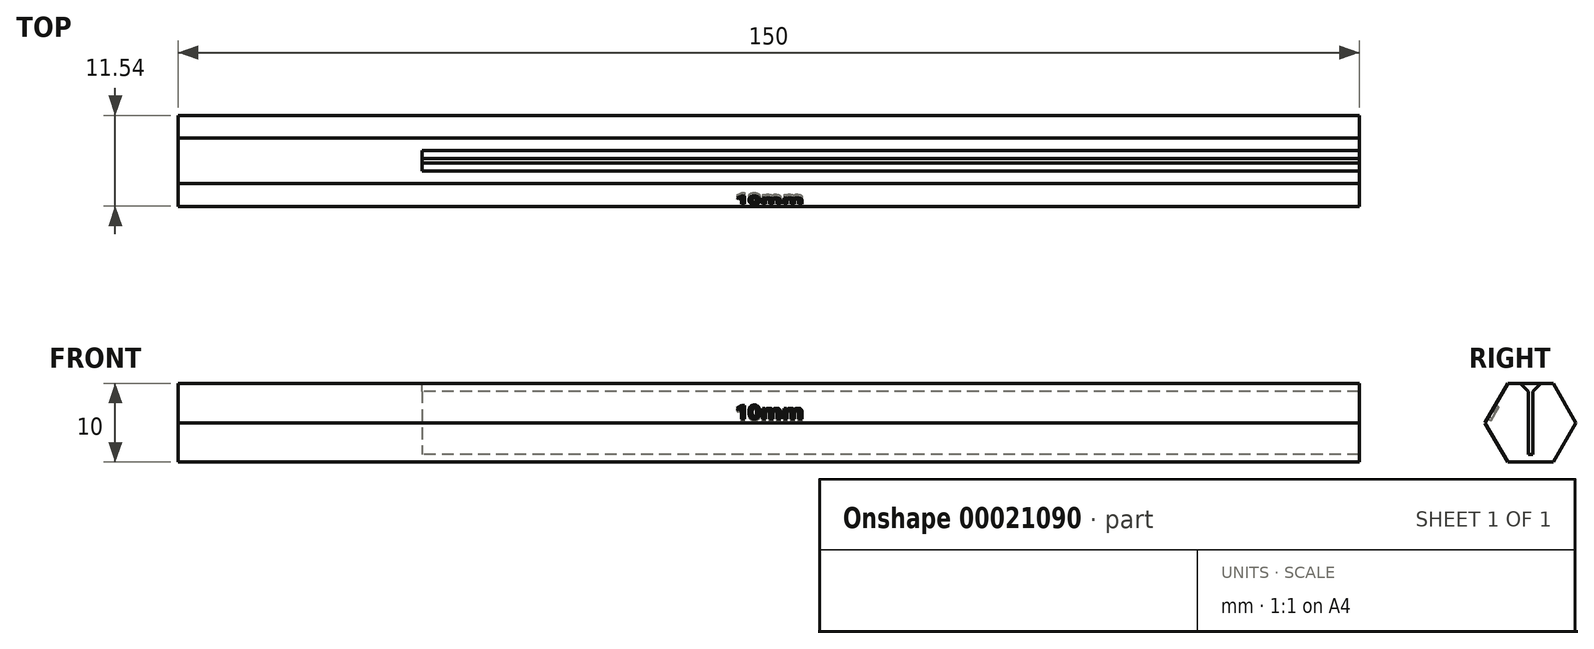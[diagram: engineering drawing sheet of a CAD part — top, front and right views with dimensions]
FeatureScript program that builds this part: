
annotation { "Feature Type Name" : "Feature", "Feature Type Description" : "" }
export const myFeature = defineFeature(function(context is Context, id is Id, definition is map)
    precondition{}
    {
        {
            var Q0;
            Q0=qCreatedBy(makeId("Right.planeOp"),FACE);
            var sketch = newSketch(context, id + "F0", { "sketchPlane" : qUnion([Q0])});
            skCircle(sketch, "E0.cCircle", {"center": v(0, 5) * mm, "radius": 5 * mm, "construction": true});
            skLineSegment(sketch, "E0.0", {"start": v(2.89, 10) * mm, "end": v(5.77, 5) * mm});
            skLineSegment(sketch, "E0.1", {"start": v(5.77, 5) * mm, "end": v(2.89, 0) * mm});
            skLineSegment(sketch, "E0.2", {"start": v(2.89, 0) * mm, "end": v(-2.89, 0) * mm});
            skLineSegment(sketch, "E0.3", {"start": v(-2.89, 0) * mm, "end": v(-5.77, 5) * mm});
            skLineSegment(sketch, "E0.4", {"start": v(-5.77, 5) * mm, "end": v(-2.89, 10) * mm});
            skLineSegment(sketch, "E0.5", {"start": v(-2.89, 10) * mm, "end": v(2.89, 10) * mm});
            skPoint(sketch, "E0.0.midPoint", {"position": v(4.33, 7.5) * mm});
            skLineSegment(sketch, "E1", {"start": v(-3.46, 1) * mm, "end": v(3.46, 1) * mm});
            skLineSegment(sketch, "E2", {"start": v(0, 0) * mm, "end": v(0, 10) * mm, "construction": true});
            skLineSegment(sketch, "E3", {"start": v(-0.3, 10) * mm, "end": v(-0.3, 0) * mm});
            skLineSegment(sketch, "E4.MirrorCS", {"start": v(0.3, 10) * mm, "end": v(0.3, 0) * mm});
            skSolve(sketch);
        }
        {
            assignVariable(context, id + "F1", {"name" : "Length", "anyValue" : 120});
        }
        {
            var Q0;
            {var subQ7=sQuery(id+"F0.wireOp",EDGE,"E0.4");Q0=makeQuery(id+"F0.imprint","IMPRINT",FACE,{"disambiguationData":[TD([[makeQuery(id+"F0.imprint","IMPRINT",EDGE,{"derivedFrom":subQ7}),-1.0]])]});}
            var Q1;
            {var subQ7=sQuery(id+"F0.wireOp",EDGE,"E0.0");Q1=makeQuery(id+"F0.imprint","IMPRINT",FACE,{"disambiguationData":[TD([[makeQuery(id+"F0.imprint","IMPRINT",EDGE,{"derivedFrom":subQ7}),-1.0]])]});}
            var Q2;
            {var subQ3=sQuery(id+"F0.wireOp",EDGE,"E0.2");var subQ5=sQuery(id+"F0.wireOp",EDGE,"E0.3");var subQ7=makeQuery(id+"F0.imprint","INTERSECT",VERTEX,{"derivedFrom":[subQ3,subQ5]});Q2=makeQuery(id+"F0.imprint","IMPRINT",FACE,{"disambiguationData":[TD([[makeQuery(id+"F0.imprint","IMPRINT",EDGE,{"disambiguationData":[TD([[subQ7,1.0]])],"derivedFrom":subQ3}),-1.0]])]});}
            var Q3;
            {var subQ3=sQuery(id+"F0.wireOp",EDGE,"E0.2");var subQ5=sQuery(id+"F0.wireOp",EDGE,"E3");var subQ7=makeQuery(id+"F0.imprint","INTERSECT",VERTEX,{"derivedFrom":[subQ3,subQ5]});Q3=makeQuery(id+"F0.imprint","IMPRINT",FACE,{"disambiguationData":[TD([[makeQuery(id+"F0.imprint","IMPRINT",EDGE,{"disambiguationData":[TD([[subQ7,1.0]])],"derivedFrom":subQ3}),-1.0]])]});}
            var Q4;
            {var subQ3=sQuery(id+"F0.wireOp",EDGE,"E0.2");var subQ5=sQuery(id+"F0.wireOp",EDGE,"E0.1");var subQ7=makeQuery(id+"F0.imprint","INTERSECT",VERTEX,{"derivedFrom":[subQ5,subQ3]});Q4=makeQuery(id+"F0.imprint","IMPRINT",FACE,{"disambiguationData":[TD([[makeQuery(id+"F0.imprint","IMPRINT",EDGE,{"disambiguationData":[TD([[subQ7,1.0]])],"derivedFrom":subQ5}),-1.0]])]});}
            extrude(context, id + "F2", {"entities" : qUnion([Q0, Q1, Q2, Q3, Q4]), "depth" : (getVariable(context, 'Length')) * mm});
        }
        {
            var Q0;
            {var subQ0=sQuery(id+"F0.wireOp",EDGE,"E3");var subQ3=sQuery(id+"F0.wireOp",EDGE,"E0.5");var subQ4=makeQuery(id+"F0.imprint","INTERSECT",VERTEX,{"derivedFrom":[subQ3,subQ0]});Q0=makeQuery(id+"F0.imprint","IMPRINT",FACE,{"disambiguationData":[TD([[makeQuery(id+"F0.imprint","IMPRINT",EDGE,{"disambiguationData":[TD([[subQ4,-1.0]])],"derivedFrom":subQ3}),-1.0]])]});}
            var Q1;
            {var subQ3=sQuery(id+"F0.wireOp",EDGE,"E0.2");var subQ5=sQuery(id+"F0.wireOp",EDGE,"E0.1");var subQ7=makeQuery(id+"F0.imprint","INTERSECT",VERTEX,{"derivedFrom":[subQ5,subQ3]});Q1=makeQuery(id+"F0.imprint","IMPRINT",FACE,{"disambiguationData":[TD([[makeQuery(id+"F0.imprint","IMPRINT",EDGE,{"disambiguationData":[TD([[subQ7,1.0]])],"derivedFrom":subQ5}),-1.0]])]});}
            var Q2;
            {var subQ3=sQuery(id+"F0.wireOp",EDGE,"E0.2");var subQ5=sQuery(id+"F0.wireOp",EDGE,"E0.3");var subQ7=makeQuery(id+"F0.imprint","INTERSECT",VERTEX,{"derivedFrom":[subQ3,subQ5]});Q2=makeQuery(id+"F0.imprint","IMPRINT",FACE,{"disambiguationData":[TD([[makeQuery(id+"F0.imprint","IMPRINT",EDGE,{"disambiguationData":[TD([[subQ7,1.0]])],"derivedFrom":subQ3}),-1.0]])]});}
            var Q3;
            {var subQ7=sQuery(id+"F0.wireOp",EDGE,"E0.0");Q3=makeQuery(id+"F0.imprint","IMPRINT",FACE,{"disambiguationData":[TD([[makeQuery(id+"F0.imprint","IMPRINT",EDGE,{"derivedFrom":subQ7}),-1.0]])]});}
            var Q4;
            {var subQ7=sQuery(id+"F0.wireOp",EDGE,"E0.4");Q4=makeQuery(id+"F0.imprint","IMPRINT",FACE,{"disambiguationData":[TD([[makeQuery(id+"F0.imprint","IMPRINT",EDGE,{"derivedFrom":subQ7}),-1.0]])]});}
            var Q5;
            {var subQ3=sQuery(id+"F0.wireOp",EDGE,"E0.2");var subQ5=sQuery(id+"F0.wireOp",EDGE,"E3");var subQ7=makeQuery(id+"F0.imprint","INTERSECT",VERTEX,{"derivedFrom":[subQ3,subQ5]});Q5=makeQuery(id+"F0.imprint","IMPRINT",FACE,{"disambiguationData":[TD([[makeQuery(id+"F0.imprint","IMPRINT",EDGE,{"disambiguationData":[TD([[subQ7,1.0]])],"derivedFrom":subQ3}),-1.0]])]});}
            extrude(context, id + "F3", {"entities" : qUnion([Q0, Q1, Q2, Q3, Q4, Q5]), "operationType" : NewBodyOperationType.ADD, "oppositeDirection" : true, "depth" : 30 * mm, "hasSecondDirection" : true, "secondDirectionOppositeDirection" : false, "secondDirectionDepth" : 1 * mm});
        }
        {
            var Q0;
            Q0=makeQuery(id+"F2.opExtrude","SWEPT_EDGE",EDGE,{"disambiguationData":[OSD([sQuery(id+"F0.wireOp",EDGE,"E0.5"),sQuery(id+"F0.wireOp",EDGE,"E3")])]});
            var Q1;
            Q1=makeQuery(id+"F2.opExtrude","SWEPT_EDGE",EDGE,{"disambiguationData":[OSD([sQuery(id+"F0.wireOp",EDGE,"E0.5"),sQuery(id+"F0.wireOp",EDGE,"E4.MirrorCS")])]});
            chamfer(context, id + "F4", {"entities" : qUnion([Q0, Q1]), "width" : 1 * mm, "tangentPropagation" : true});
        }
        {
            var Q0;
            {var subQ0=sQuery(id+"F0.wireOp",EDGE,"E0.4");Q0=makeQuery(id+"F3.boolean.opBoolean","MERGE",FACE,{"derivedFrom":[makeQuery(id+"F2.opExtrude","SWEPT_FACE",FACE,{"disambiguationData":[OSD([subQ0])]}),makeQuery(id+"F3.opExtrude","SWEPT_FACE",FACE,{"disambiguationData":[OSD([subQ0])]})]});}
            var sketch = newSketch(context, id + "F5", { "sketchPlane" : qUnion([Q0])});
            skLineSegment(sketch, "E5.0", {"start": v(-30, 1.44) * mm, "end": v(-30, 7.22) * mm, "construction": true});
            skLineSegment(sketch, "E5.1", {"start": v(120, 1.44) * mm, "end": v(-30, 1.44) * mm, "construction": true});
            skLineSegment(sketch, "E5.2", {"start": v(120, 7.22) * mm, "end": v(-30, 7.22) * mm, "construction": true});
            skLineSegment(sketch, "E5.3", {"start": v(120, 1.44) * mm, "end": v(120, 7.22) * mm, "construction": true});
            skText(sketch, "E6", { "text": "10mm", "fontName": "OpenSans-Bold.ttf"});
            skLineSegment(sketch, "E7", {"start": v(120, 4.33) * mm, "end": v(-30, 4.33) * mm, "construction": true});
            skLineSegment(sketch, "E8", {"start": v(45, 7.22) * mm, "end": v(45, 1.44) * mm, "construction": true});
            skPoint(sketch, "E9", {"position": v(40.8, 4.33) * mm});
            const initialGuessF5  = {"E6": [0.0408, 0.00203, 1, 0, 0.002]};
            skSetInitialGuess(sketch, initialGuessF5);
            skSolve(sketch);
        }
        {
            var Q0;
            Q0=qSketchRegion(id+"F5",true);
            extrude(context, id + "F6", {"entities" : qUnion([Q0]), "operationType" : NewBodyOperationType.REMOVE, "oppositeDirection" : true, "depth" : .5 * mm});
        }
    });
